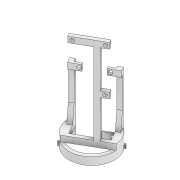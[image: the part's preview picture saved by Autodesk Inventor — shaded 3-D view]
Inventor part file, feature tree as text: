
AUTODESK INVENTOR PART (.ipt)
format: ipt  version: 2022.3 (Build 263350000, 350)  size: 320,512 bytes
history: native  units: mm
features: extrude x12, sketch x12, chamfer x2, other x1, projected_geometry x1
ambient origin geometry x8: Origin, YZ Plane, XZ Plane, XY Plane, X Axis, Y Axis, Z Axis, Center Point
bodies: Body1 (feature_tree)
feature tree (28):
  other  "Sólido1"
  extrude  "Extrusión1"  Depth=0.25mm
  extrude  "Extrusión2"  Depth=1.0mm
  extrude  "Extrusión3"  Depth=6.5mm
  extrude  "Extrusión4"  Depth=2.0mm
  extrude  "Extrusión5"  Depth=2.4mm
  chamfer  "Chaflán1"  Distance=1.0mm
  chamfer  "Chaflán2"  Distance=5.0mm
  extrude  "Extrusión6"  Depth=2.0mm
  extrude  "Extrusión7"  Depth=14.0mm TaperAngle=15.0deg
  extrude  "Extrusión8"  Depth=2.0mm
  extrude  "Extrusión9"  Depth=9.0mm
  extrude  "Extrusión10"  Depth=10.0mm
  extrude  "Extrusión11"  Depth=10.0mm
  extrude  "Extrusión12"  Depth=3.0mm
  sketch  "Boceto1"  dims[d0=39.5mm d1=0.25mm]
  sketch  "Boceto2"  dims[d2=33.5mm d3=1.0mm]
  sketch  "Boceto3"  dims[d4=6.5mm d5=0.0mm d6=39.5mm d7=0.25mm d8=33.5mm d9=1.0mm]
  sketch  "Boceto5"  dims[d10=2.0mm d11=2.0mm]
  sketch  "Boceto7"  dims[d12=2.4mm d13=0.0mm d14=7.0mm]
  sketch  "Boceto8"  dims[d15=3.0mm d16=1.0mm d17=0.0mm]
  sketch  "Boceto9"  dims[d18=18.0mm d19=5.0mm d20=0.0mm]
  sketch  "Boceto10"  dims[d22=3.0mm d23=2.0mm]
  sketch  "Boceto11"  dims[d24=45.0mm d25=0.0mm d26=14.0mm d27=2.0mm d28=15.0deg]
  sketch  "Boceto12"  dims[d29=14.0mm d30=2.0mm d31=15.0deg d32=2.0mm]
  projected_geometry  "Contorno proyectado3"
  sketch  "Boceto13"  dims[d33=9.0mm d34=9.0mm]
  sketch  "Boceto14"  dims[d35=5.0mm d36=0.0mm d37=10.0mm d38=10.0mm d39=3.0mm d40=3.0mm d41=5.0mm d42=0.0mm d43=10.0mm d44=4.0mm d45=75.0mm d46=0.0mm d47=5.0mm d48=6.0mm d49=0.0mm d50=16.5mm d51=0.0mm d52=10.5mm d53=10.5mm d54=3.0mm d55=3.0mm d56=0.0mm d57=0.0mm d58=32.3mm d59=6.0mm d60=5.0mm d61=90.0deg d62=3.0mm d63=3.0mm d64=0.0mm]
